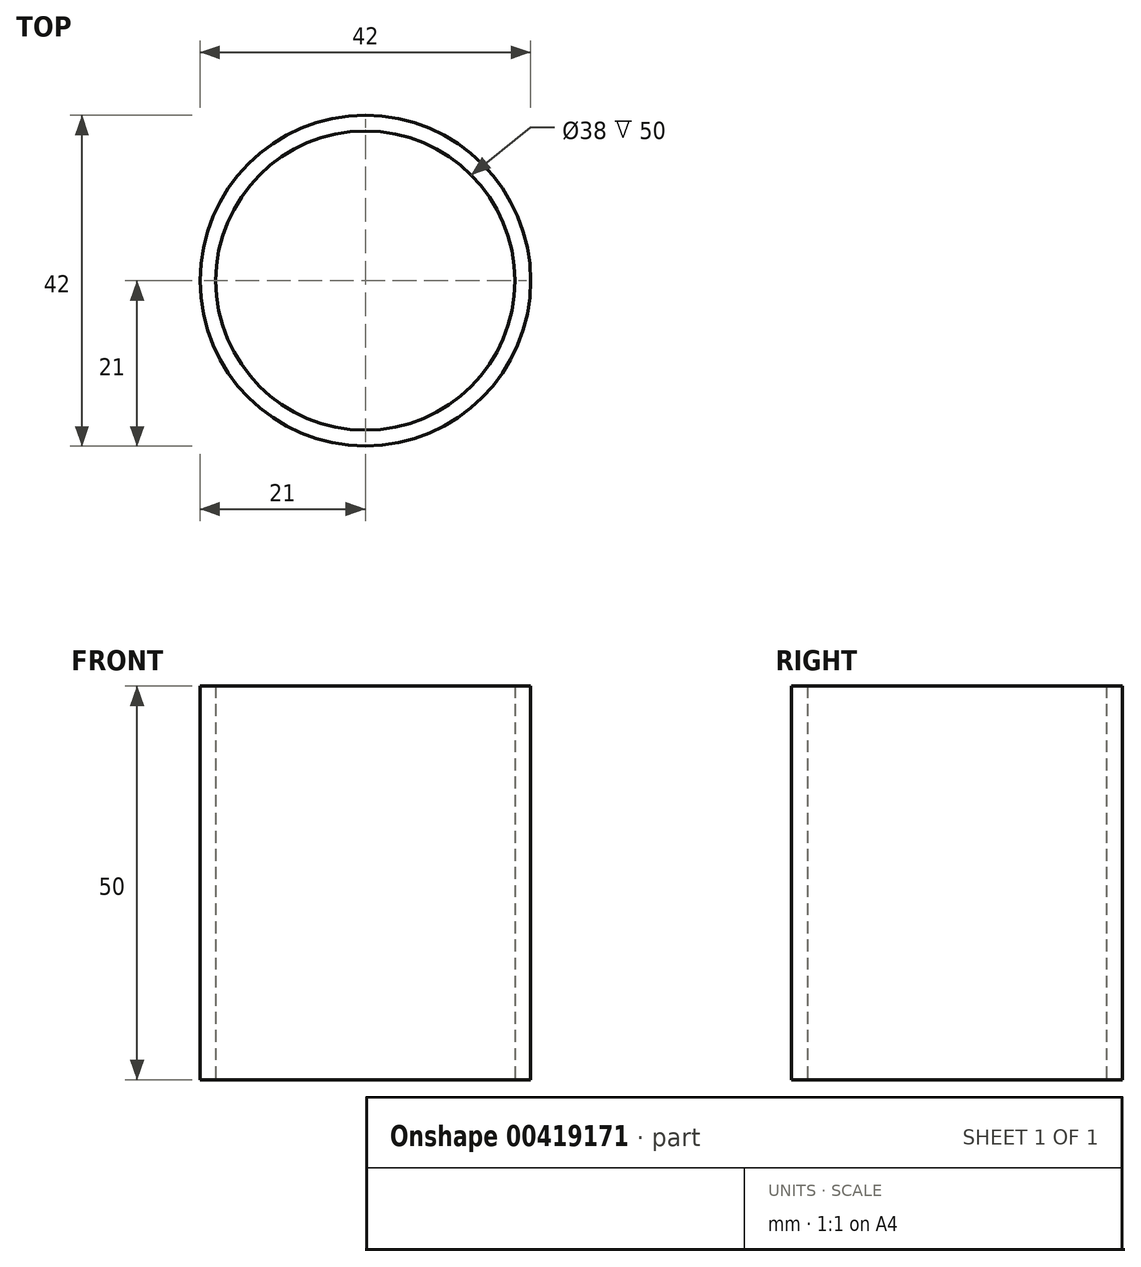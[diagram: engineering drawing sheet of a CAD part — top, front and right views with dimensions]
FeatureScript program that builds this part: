
annotation { "Feature Type Name" : "Feature", "Feature Type Description" : "" }
export const myFeature = defineFeature(function(context is Context, id is Id, definition is map)
    precondition{}
    {
        {
            var Q0;
            Q0=qCreatedBy(makeId("Top.planeOp"),FACE);
            var sketch = newSketch(context, id + "F0", { "sketchPlane" : qUnion([Q0])});
            skCircle(sketch, "E0", {"center": v(0, 0) * mm, "radius": 19 * mm});
            skCircle(sketch, "E1", {"center": v(0, 0) * mm, "radius": 21 * mm});
            skSolve(sketch);
        }
        {
            var Q0;
            Q0 = qSketchRegion(id + "F0", true);
            extrude(context, id + "F1", {"entities" : qUnion([Q0]), "depth" : 50 * mm});
        }
    });
